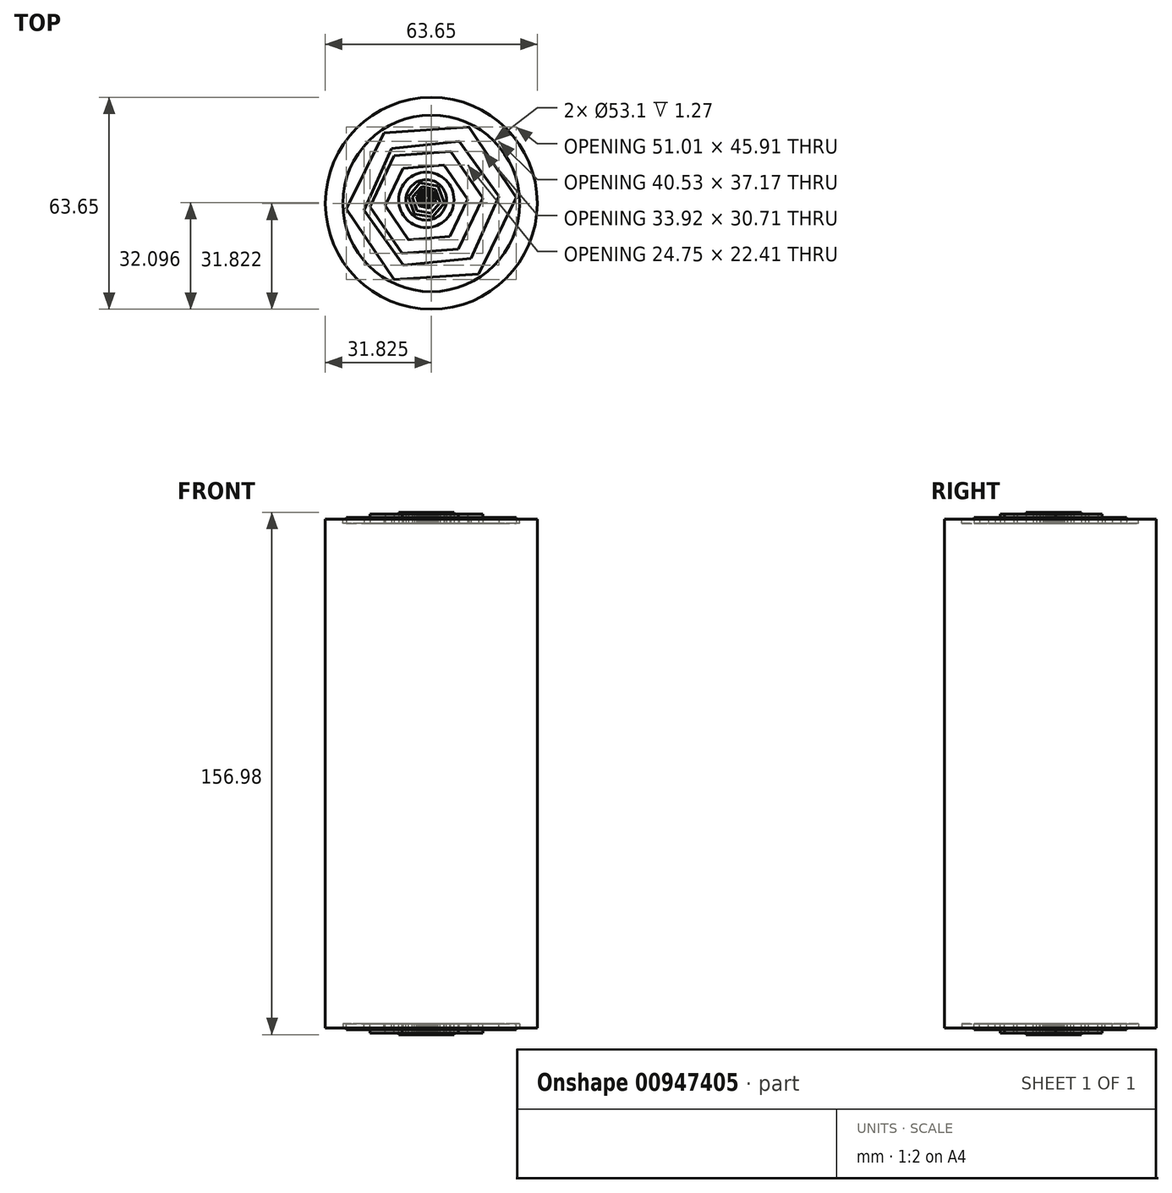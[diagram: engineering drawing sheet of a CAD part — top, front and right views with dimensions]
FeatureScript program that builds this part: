
annotation { "Feature Type Name" : "Feature", "Feature Type Description" : "" }
export const myFeature = defineFeature(function(context is Context, id is Id, definition is map)
    precondition{}
    {
        {
            var Q0;
            Q0=qCreatedBy(makeId("Top.planeOp"),FACE);
            var sketch = newSketch(context, id + "F0", { "sketchPlane" : qUnion([Q0])});
            skLineSegment(sketch, "E0.bottom", {"start": v(-51.93, 60.76) * mm, "end": v(61.08, 60.76) * mm});
            skLineSegment(sketch, "E0.top", {"start": v(-51.93, -63.18) * mm, "end": v(61.08, -63.18) * mm});
            skLineSegment(sketch, "E0.left", {"start": v(-51.93, 60.76) * mm, "end": v(-51.93, -63.18) * mm});
            skLineSegment(sketch, "E0.right", {"start": v(61.08, 60.76) * mm, "end": v(61.08, -63.18) * mm});
            skSolve(sketch);
        }
        {
            var Q0;
            Q0 = qSketchRegion(id + "F0", true);
            var Q1;
            Q1=sQuery(id+"F0.wireOp",EDGE,"E0.left");
            extrude(context, id + "F1", {"entities" : qUnion([Q0]), "surfaceEntities" : qUnion([Q1]), "depth" : 76.45 * mm, "offsetDistance" : 25.4 * mm});
        }
        {
            var Q0;
            Q0=makeQuery(id+"F1.opExtrude","CAP_FACE",FACE,{"disambiguationData":[OSD([sQuery(id+"F0.wireOp",EDGE,"E0.bottom"),sQuery(id+"F0.wireOp",EDGE,"E0.top"),sQuery(id+"F0.wireOp",EDGE,"E0.left"),sQuery(id+"F0.wireOp",EDGE,"E0.right")])],"isStart":false});
            var sketch = newSketch(context, id + "F2", { "sketchPlane" : qUnion([Q0])});
            skLineSegment(sketch, "E1", {"start": v(-51.93, 0) * mm, "end": v(-14.1, 60.76) * mm});
            skPoint(sketch, "E1.startSnap0", {"position": v(-51.93, -1.2) * mm});
            skLineSegment(sketch, "E2", {"start": v(-14.1, 60.76) * mm, "end": v(-51.93, 60.76) * mm});
            skLineSegment(sketch, "E3", {"start": v(-51.93, 60.76) * mm, "end": v(-51.93, -1.2) * mm});
            skSolve(sketch);
        }
        {
            var Q0;
            Q0 = qSketchRegion(id + "F2", true);
            extrude(context, id + "F3", {"entities" : qUnion([Q0]), "operationType" : NewBodyOperationType.REMOVE, "oppositeDirection" : true, "depth" : 101.1 * mm, "offsetDistance" : 25.4 * mm});
        }
        {
            var Q0;
            Q0=makeQuery(id+"F1.opExtrude","CAP_FACE",FACE,{"disambiguationData":[OSD([sQuery(id+"F0.wireOp",EDGE,"E0.bottom"),sQuery(id+"F0.wireOp",EDGE,"E0.top"),sQuery(id+"F0.wireOp",EDGE,"E0.left"),sQuery(id+"F0.wireOp",EDGE,"E0.right")])],"isStart":false});
            var sketch = newSketch(context, id + "F4", { "sketchPlane" : qUnion([Q0])});
            skLineSegment(sketch, "E4", {"start": v(61.08, 0) * mm, "end": v(13.5, 60.76) * mm});
            skLineSegment(sketch, "E5", {"start": v(13.5, 60.76) * mm, "end": v(61.08, 60.76) * mm});
            skLineSegment(sketch, "E6", {"start": v(61.08, 60.76) * mm, "end": v(61.08, 0) * mm});
            skSolve(sketch);
        }
        {
            var Q0;
            Q0 = qSketchRegion(id + "F4", true);
            extrude(context, id + "F5", {"entities" : qUnion([Q0]), "operationType" : NewBodyOperationType.REMOVE, "oppositeDirection" : true, "depth" : 99.57 * mm, "offsetDistance" : 25.4 * mm});
        }
        {
            var Q0;
            Q0=makeQuery(id+"F1.opExtrude","CAP_FACE",FACE,{"disambiguationData":[OSD([sQuery(id+"F0.wireOp",EDGE,"E0.bottom"),sQuery(id+"F0.wireOp",EDGE,"E0.top"),sQuery(id+"F0.wireOp",EDGE,"E0.left"),sQuery(id+"F0.wireOp",EDGE,"E0.right")])],"isStart":false});
            var sketch = newSketch(context, id + "F6", { "sketchPlane" : qUnion([Q0])});
            skLineSegment(sketch, "E7", {"start": v(-51.93, 0) * mm, "end": v(-0.3, 60.76) * mm});
            skLineSegment(sketch, "E8", {"start": v(-0.3, 60.76) * mm, "end": v(61.08, 0) * mm});
            skLineSegment(sketch, "E9", {"start": v(61.08, 0) * mm, "end": v(13.5, 60.76) * mm});
            skLineSegment(sketch, "E10", {"start": v(13.5, 60.76) * mm, "end": v(-14.1, 60.76) * mm});
            skLineSegment(sketch, "E11", {"start": v(-14.1, 60.76) * mm, "end": v(-51.93, 0) * mm});
            skSolve(sketch);
        }
        {
            var Q0;
            Q0 = qSketchRegion(id + "F6", true);
            extrude(context, id + "F7", {"entities" : qUnion([Q0]), "operationType" : NewBodyOperationType.REMOVE, "oppositeDirection" : true, "depth" : 103.38 * mm, "offsetDistance" : 25.4 * mm});
        }
        {
            var Q0;
            Q0=makeQuery(id+"F1.opExtrude","CAP_FACE",FACE,{"disambiguationData":[OSD([sQuery(id+"F0.wireOp",EDGE,"E0.bottom"),sQuery(id+"F0.wireOp",EDGE,"E0.top"),sQuery(id+"F0.wireOp",EDGE,"E0.left"),sQuery(id+"F0.wireOp",EDGE,"E0.right")])],"isStart":false});
            var sketch = newSketch(context, id + "F8", { "sketchPlane" : qUnion([Q0])});
            skLineSegment(sketch, "E12", {"start": v(-11.92, -63.18) * mm, "end": v(-11.92, -38.13) * mm});
            skLineSegment(sketch, "E13", {"start": v(-11.92, -38.13) * mm, "end": v(0, -38.13) * mm});
            skLineSegment(sketch, "E14", {"start": v(0, -38.13) * mm, "end": v(0, -63.18) * mm});
            skLineSegment(sketch, "E15", {"start": v(0, -63.18) * mm, "end": v(12.9, -63.18) * mm});
            skLineSegment(sketch, "E16", {"start": v(12.9, -63.18) * mm, "end": v(12.9, -38.13) * mm});
            skLineSegment(sketch, "E17", {"start": v(12.9, -38.13) * mm, "end": v(0, -38.13) * mm});
            skLineSegment(sketch, "E18", {"start": v(-11.92, -63.18) * mm, "end": v(0, -63.18) * mm});
            skSolve(sketch);
        }
        {
            var Q0;
            Q0 = qSketchRegion(id + "F8", true);
            extrude(context, id + "F9", {"entities" : qUnion([Q0]), "operationType" : NewBodyOperationType.REMOVE, "oppositeDirection" : true, "depth" : 2.3 * mm, "offsetDistance" : 25.4 * mm});
        }
        {
            var Q0;
            {var subQ0=sQuery(id+"F8.wireOp",EDGE,"E12");var subQ1=sQuery(id+"F8.wireOp",EDGE,"E17");var subQ2=sQuery(id+"F8.wireOp",EDGE,"E13");Q0=makeQuery(id+"FAAV3g0l9lUvfrH_1.boolean.opBoolean","SPLIT",FACE,{"disambiguationData":[TD([makeQuery(id+"F9.boolean.opBoolean","COPY",FACE,{"derivedFrom":makeQuery(id+"F9.opExtrude","SWEPT_FACE",FACE,{"disambiguationData":[OSD([subQ0])]})})])],"derivedFrom":makeQuery(id+"F9.boolean.opBoolean","COPY",FACE,{"derivedFrom":makeQuery(id+"F9.opExtrude","CAP_FACE",FACE,{"disambiguationData":[OSD([subQ0,subQ2,sQuery(id+"F8.wireOp",EDGE,"E15"),sQuery(id+"F8.wireOp",EDGE,"E16"),subQ1,sQuery(id+"F8.wireOp",EDGE,"E18")])],"isStart":false})})});}
            var sketch = newSketch(context, id + "F10", { "sketchPlane" : qUnion([Q0])});
            skCircle(sketch, "E19", {"center": v(-1.35, -50.28) * mm, "radius": 0.62 * mm});
            skCircle(sketch, "E20", {"center": v(1.89, -50.24) * mm, "radius": 0.62 * mm});
            skSolve(sketch);
        }
        {
            var Q0;
            Q0 = qSketchRegion(id + "F10", true);
            extrude(context, id + "F11", {"entities" : qUnion([Q0]), "operationType" : NewBodyOperationType.ADD, "depth" : 0.69 * mm, "offsetDistance" : 25.4 * mm});
        }
        {
            var Q0;
            Q0=makeQuery(id+"F1.opExtrude","CAP_FACE",FACE,{"disambiguationData":[OSD([sQuery(id+"F0.wireOp",EDGE,"E0.bottom"),sQuery(id+"F0.wireOp",EDGE,"E0.top"),sQuery(id+"F0.wireOp",EDGE,"E0.left"),sQuery(id+"F0.wireOp",EDGE,"E0.right")])],"isStart":false});
            var sketch = newSketch(context, id + "F12", { "sketchPlane" : qUnion([Q0])});
            skCircle(sketch, "E21", {"center": v(1.5, 13.2) * mm, "radius": 26.55 * mm});
            skSolve(sketch);
        }
        {
            var Q0;
            Q0 = qSketchRegion(id + "F12", true);
            extrude(context, id + "F13", {"entities" : qUnion([Q0]), "operationType" : NewBodyOperationType.REMOVE, "oppositeDirection" : true, "depth" : 1.27 * mm, "offsetDistance" : 25.4 * mm});
        }
        {
            var Q0;
            Q0=makeQuery(id+"F13.boolean.opBoolean","COPY",FACE,{"derivedFrom":makeQuery(id+"F13.opExtrude","CAP_FACE",FACE,{"disambiguationData":[OSD([sQuery(id+"F12.wireOp",EDGE,"E21")])],"isStart":false})});
            var sketch = newSketch(context, id + "F14", { "sketchPlane" : qUnion([Q0])});
            skCircle(sketch, "E22.cCircle", {"center": v(1.5, 13.2) * mm, "radius": 22.14 * mm, "construction": true});
            skLineSegment(sketch, "E22.0", {"start": v(-12.75, 34.42) * mm, "end": v(12.75, 36.16) * mm});
            skLineSegment(sketch, "E22.1", {"start": v(12.75, 36.16) * mm, "end": v(27, 14.94) * mm});
            skLineSegment(sketch, "E22.2", {"start": v(27, 14.94) * mm, "end": v(15.76, -8.02) * mm});
            skLineSegment(sketch, "E22.3", {"start": v(15.76, -8.02) * mm, "end": v(-9.74, -9.75) * mm});
            skLineSegment(sketch, "E22.4", {"start": v(-9.74, -9.75) * mm, "end": v(-24, 11.47) * mm});
            skLineSegment(sketch, "E22.5", {"start": v(-24, 11.47) * mm, "end": v(-12.75, 34.42) * mm});
            skPoint(sketch, "E22.0.midPoint", {"position": v(0, 35.29) * mm});
            skCircle(sketch, "E23.cCircle", {"center": v(1.5, 13.2) * mm, "radius": 17.64 * mm, "construction": true});
            skLineSegment(sketch, "E23.0", {"start": v(-18.76, 11.13) * mm, "end": v(-10.43, 29.71) * mm});
            skLineSegment(sketch, "E23.1", {"start": v(-10.43, 29.71) * mm, "end": v(9.84, 31.79) * mm});
            skLineSegment(sketch, "E23.2", {"start": v(9.84, 31.79) * mm, "end": v(21.77, 15.28) * mm});
            skLineSegment(sketch, "E23.3", {"start": v(21.77, 15.28) * mm, "end": v(13.43, -3.3) * mm});
            skLineSegment(sketch, "E23.4", {"start": v(13.43, -3.3) * mm, "end": v(-6.83, -5.38) * mm});
            skLineSegment(sketch, "E23.5", {"start": v(-6.83, -5.38) * mm, "end": v(-18.76, 11.13) * mm});
            skPoint(sketch, "E23.0.midPoint", {"position": v(-14.6, 20.42) * mm});
            skSolve(sketch);
        }
        {
            var Q0;
            Q0 = qSketchRegion(id + "F14", true);
            extrude(context, id + "F15", {"entities" : qUnion([Q0]), "operationType" : NewBodyOperationType.ADD, "depth" : 1.78 * mm, "offsetDistance" : 25.4 * mm});
        }
        {
            var Q0;
            Q0=makeQuery(id+"F15.boolean.opBoolean","SPLIT",FACE,{"disambiguationData":[TD([makeQuery(id+"F15.opExtrude","SWEPT_FACE",FACE,{"disambiguationData":[OSD([sQuery(id+"F14.wireOp",EDGE,"E23.0")])]})])],"derivedFrom":makeQuery(id+"F13.boolean.opBoolean","COPY",FACE,{"derivedFrom":makeQuery(id+"F13.opExtrude","CAP_FACE",FACE,{"disambiguationData":[OSD([sQuery(id+"F12.wireOp",EDGE,"E21")])],"isStart":false})})});
            var sketch = newSketch(context, id + "F16", { "sketchPlane" : qUnion([Q0])});
            skCircle(sketch, "E24.cCircle", {"center": v(0, 13.48) * mm, "radius": 14.73 * mm, "construction": true});
            skLineSegment(sketch, "E24.0", {"start": v(-7.32, -1.88) * mm, "end": v(-16.96, 12.14) * mm});
            skLineSegment(sketch, "E24.1", {"start": v(-16.96, 12.14) * mm, "end": v(-9.64, 27.5) * mm});
            skLineSegment(sketch, "E24.2", {"start": v(-9.64, 27.5) * mm, "end": v(7.32, 28.83) * mm});
            skLineSegment(sketch, "E24.3", {"start": v(7.32, 28.83) * mm, "end": v(16.96, 14.81) * mm});
            skLineSegment(sketch, "E24.4", {"start": v(16.96, 14.81) * mm, "end": v(9.64, -0.54) * mm});
            skLineSegment(sketch, "E24.5", {"start": v(9.64, -0.54) * mm, "end": v(-7.32, -1.88) * mm});
            skPoint(sketch, "E24.0.midPoint", {"position": v(-12.14, 5.13) * mm});
            skCircle(sketch, "E25.cCircle", {"center": v(0, 13.48) * mm, "radius": 10.75 * mm, "construction": true});
            skLineSegment(sketch, "E25.0", {"start": v(-5.34, 2.27) * mm, "end": v(-12.37, 12.5) * mm});
            skLineSegment(sketch, "E25.1", {"start": v(-12.37, 12.5) * mm, "end": v(-7.03, 23.7) * mm});
            skLineSegment(sketch, "E25.2", {"start": v(-7.03, 23.7) * mm, "end": v(5.34, 24.68) * mm});
            skLineSegment(sketch, "E25.3", {"start": v(5.34, 24.68) * mm, "end": v(12.37, 14.45) * mm});
            skLineSegment(sketch, "E25.4", {"start": v(12.37, 14.45) * mm, "end": v(7.03, 3.25) * mm});
            skLineSegment(sketch, "E25.5", {"start": v(7.03, 3.25) * mm, "end": v(-5.34, 2.27) * mm});
            skPoint(sketch, "E25.0.midPoint", {"position": v(-8.86, 7.39) * mm});
            skSolve(sketch);
        }
        {
            var Q0;
            Q0 = qSketchRegion(id + "F16", true);
            extrude(context, id + "F17", {"entities" : qUnion([Q0]), "operationType" : NewBodyOperationType.ADD, "depth" : 2.8 * mm, "offsetDistance" : 25.4 * mm});
        }
        {
            var Q0;
            Q0=makeQuery(id+"F17.boolean.opBoolean","SPLIT",FACE,{"disambiguationData":[TD([makeQuery(id+"F17.opExtrude","SWEPT_FACE",FACE,{"disambiguationData":[OSD([sQuery(id+"F16.wireOp",EDGE,"E25.0")])]})])],"derivedFrom":makeQuery(id+"F15.boolean.opBoolean","SPLIT",FACE,{"disambiguationData":[TD([makeQuery(id+"F15.opExtrude","SWEPT_FACE",FACE,{"disambiguationData":[OSD([sQuery(id+"F14.wireOp",EDGE,"E23.0")])]})])],"derivedFrom":makeQuery(id+"F13.boolean.opBoolean","COPY",FACE,{"derivedFrom":makeQuery(id+"F13.opExtrude","CAP_FACE",FACE,{"disambiguationData":[OSD([sQuery(id+"F12.wireOp",EDGE,"E21")])],"isStart":false})})})});
            var sketch = newSketch(context, id + "F18", { "sketchPlane" : qUnion([Q0])});
            skCircle(sketch, "E26", {"center": v(0, 14.22) * mm, "radius": 8.33 * mm});
            skCircle(sketch, "E27", {"center": v(0, 14.22) * mm, "radius": 6.1 * mm});
            skSolve(sketch);
        }
        {
            var Q0;
            Q0 = qSketchRegion(id + "F18", true);
            extrude(context, id + "F19", {"entities" : qUnion([Q0]), "operationType" : NewBodyOperationType.ADD, "depth" : 3.3 * mm, "offsetDistance" : 25.4 * mm});
        }
        {
            var Q0;
            Q0=makeQuery(id+"F19.boolean.opBoolean","SPLIT",FACE,{"disambiguationData":[TD([makeQuery(id+"F19.opExtrude","SWEPT_FACE",FACE,{"disambiguationData":[OSD([sQuery(id+"F18.wireOp",EDGE,"E27")])]})])],"derivedFrom":makeQuery(id+"F17.boolean.opBoolean","SPLIT",FACE,{"disambiguationData":[TD([makeQuery(id+"F17.opExtrude","SWEPT_FACE",FACE,{"disambiguationData":[OSD([sQuery(id+"F16.wireOp",EDGE,"E25.0")])]})])],"derivedFrom":makeQuery(id+"F15.boolean.opBoolean","SPLIT",FACE,{"disambiguationData":[TD([makeQuery(id+"F15.opExtrude","SWEPT_FACE",FACE,{"disambiguationData":[OSD([sQuery(id+"F14.wireOp",EDGE,"E23.0")])]})])],"derivedFrom":makeQuery(id+"F13.boolean.opBoolean","COPY",FACE,{"derivedFrom":makeQuery(id+"F13.opExtrude","CAP_FACE",FACE,{"disambiguationData":[OSD([sQuery(id+"F12.wireOp",EDGE,"E21")])],"isStart":false})})})})});
            var sketch = newSketch(context, id + "F20", { "sketchPlane" : qUnion([Q0])});
            skCircle(sketch, "E28.cCircle", {"center": v(0, 14.22) * mm, "radius": 4.75 * mm, "construction": true});
            skLineSegment(sketch, "E28.0", {"start": v(-5.49, 14.02) * mm, "end": v(-2.92, 18.87) * mm});
            skLineSegment(sketch, "E28.1", {"start": v(-2.92, 18.87) * mm, "end": v(2.57, 19.07) * mm});
            skLineSegment(sketch, "E28.2", {"start": v(2.57, 19.07) * mm, "end": v(5.49, 14.42) * mm});
            skLineSegment(sketch, "E28.3", {"start": v(5.49, 14.42) * mm, "end": v(2.92, 9.57) * mm});
            skLineSegment(sketch, "E28.4", {"start": v(2.92, 9.57) * mm, "end": v(-2.57, 9.37) * mm});
            skLineSegment(sketch, "E28.5", {"start": v(-2.57, 9.37) * mm, "end": v(-5.49, 14.02) * mm});
            skPoint(sketch, "E28.0.midPoint", {"position": v(-4.2, 16.44) * mm});
            skCircle(sketch, "E29.cCircle", {"center": v(0, 14.22) * mm, "radius": 3.89 * mm, "construction": true});
            skLineSegment(sketch, "E29.0", {"start": v(-4.49, 14.15) * mm, "end": v(-2.3, 18.07) * mm});
            skLineSegment(sketch, "E29.1", {"start": v(-2.3, 18.07) * mm, "end": v(2.19, 18.14) * mm});
            skLineSegment(sketch, "E29.2", {"start": v(2.19, 18.14) * mm, "end": v(4.49, 14.28) * mm});
            skLineSegment(sketch, "E29.3", {"start": v(4.49, 14.28) * mm, "end": v(2.3, 10.37) * mm});
            skLineSegment(sketch, "E29.4", {"start": v(2.3, 10.37) * mm, "end": v(-2.19, 10.3) * mm});
            skLineSegment(sketch, "E29.5", {"start": v(-2.19, 10.3) * mm, "end": v(-4.49, 14.15) * mm});
            skPoint(sketch, "E29.0.midPoint", {"position": v(-3.4, 16.11) * mm});
            skSolve(sketch);
        }
        {
            var Q0;
            Q0 = qSketchRegion(id + "F20", true);
            extrude(context, id + "F21", {"entities" : qUnion([Q0]), "operationType" : NewBodyOperationType.ADD, "oppositeDirection" : true, "depth" : 3.56 * mm, "offsetDistance" : 25.4 * mm});
        }
        {
            var Q0;
            Q0=makeQuery(id+"F19.boolean.opBoolean","SPLIT",FACE,{"disambiguationData":[TD([makeQuery(id+"F19.opExtrude","SWEPT_FACE",FACE,{"disambiguationData":[OSD([sQuery(id+"F18.wireOp",EDGE,"E27")])]})])],"derivedFrom":makeQuery(id+"F17.boolean.opBoolean","SPLIT",FACE,{"disambiguationData":[TD([makeQuery(id+"F17.opExtrude","SWEPT_FACE",FACE,{"disambiguationData":[OSD([sQuery(id+"F16.wireOp",EDGE,"E25.0")])]})])],"derivedFrom":makeQuery(id+"F15.boolean.opBoolean","SPLIT",FACE,{"disambiguationData":[TD([makeQuery(id+"F15.opExtrude","SWEPT_FACE",FACE,{"disambiguationData":[OSD([sQuery(id+"F14.wireOp",EDGE,"E23.0")])]})])],"derivedFrom":makeQuery(id+"F13.boolean.opBoolean","COPY",FACE,{"derivedFrom":makeQuery(id+"F13.opExtrude","CAP_FACE",FACE,{"disambiguationData":[OSD([sQuery(id+"F12.wireOp",EDGE,"E21")])],"isStart":false})})})})});
            var sketch = newSketch(context, id + "F22", { "sketchPlane" : qUnion([Q0])});
            skCircle(sketch, "E30.cCircle", {"center": v(0, 14.22) * mm, "radius": 4.75 * mm, "construction": true});
            skLineSegment(sketch, "E30.0", {"start": v(-5.4, 15.18) * mm, "end": v(-1.87, 19.37) * mm});
            skLineSegment(sketch, "E30.1", {"start": v(-1.87, 19.37) * mm, "end": v(3.53, 18.41) * mm});
            skLineSegment(sketch, "E30.2", {"start": v(3.53, 18.41) * mm, "end": v(5.4, 13.26) * mm});
            skLineSegment(sketch, "E30.3", {"start": v(5.4, 13.26) * mm, "end": v(1.87, 9.07) * mm});
            skLineSegment(sketch, "E30.4", {"start": v(1.87, 9.07) * mm, "end": v(-3.53, 10.02) * mm});
            skLineSegment(sketch, "E30.5", {"start": v(-3.53, 10.02) * mm, "end": v(-5.4, 15.18) * mm});
            skPoint(sketch, "E30.0.midPoint", {"position": v(-3.63, 17.27) * mm});
            skCircle(sketch, "E31.cCircle", {"center": v(0, 14.22) * mm, "radius": 3.68 * mm, "construction": true});
            skLineSegment(sketch, "E31.0", {"start": v(-4.16, 15.08) * mm, "end": v(-1.33, 18.25) * mm});
            skLineSegment(sketch, "E31.1", {"start": v(-1.33, 18.25) * mm, "end": v(2.82, 17.39) * mm});
            skLineSegment(sketch, "E31.2", {"start": v(2.82, 17.39) * mm, "end": v(4.16, 13.36) * mm});
            skLineSegment(sketch, "E31.3", {"start": v(4.16, 13.36) * mm, "end": v(1.33, 10.2) * mm});
            skLineSegment(sketch, "E31.4", {"start": v(1.33, 10.2) * mm, "end": v(-2.82, 11.05) * mm});
            skLineSegment(sketch, "E31.5", {"start": v(-2.82, 11.05) * mm, "end": v(-4.16, 15.08) * mm});
            skPoint(sketch, "E31.0.midPoint", {"position": v(-2.75, 16.66) * mm});
            skSolve(sketch);
        }
        {
            var Q0;
            Q0 = qSketchRegion(id + "F22", true);
            extrude(context, id + "F23", {"entities" : qUnion([Q0]), "operationType" : NewBodyOperationType.ADD, "depth" : 3.05 * mm, "offsetDistance" : 25.4 * mm});
        }
        {
            var Q0;
            Q0=makeQuery(id+"F23.boolean.opBoolean","SPLIT",FACE,{"disambiguationData":[TD([makeQuery(id+"F23.opExtrude","SWEPT_FACE",FACE,{"disambiguationData":[OSD([sQuery(id+"F22.wireOp",EDGE,"E31.0")])]})])],"derivedFrom":makeQuery(id+"F19.boolean.opBoolean","SPLIT",FACE,{"disambiguationData":[TD([makeQuery(id+"F19.opExtrude","SWEPT_FACE",FACE,{"disambiguationData":[OSD([sQuery(id+"F18.wireOp",EDGE,"E27")])]})])],"derivedFrom":makeQuery(id+"F17.boolean.opBoolean","SPLIT",FACE,{"disambiguationData":[TD([makeQuery(id+"F17.opExtrude","SWEPT_FACE",FACE,{"disambiguationData":[OSD([sQuery(id+"F16.wireOp",EDGE,"E25.0")])]})])],"derivedFrom":makeQuery(id+"F15.boolean.opBoolean","SPLIT",FACE,{"disambiguationData":[TD([makeQuery(id+"F15.opExtrude","SWEPT_FACE",FACE,{"disambiguationData":[OSD([sQuery(id+"F14.wireOp",EDGE,"E23.0")])]})])],"derivedFrom":makeQuery(id+"F13.boolean.opBoolean","COPY",FACE,{"derivedFrom":makeQuery(id+"F13.opExtrude","CAP_FACE",FACE,{"disambiguationData":[OSD([sQuery(id+"F12.wireOp",EDGE,"E21")])],"isStart":false})})})})})});
            var sketch = newSketch(context, id + "F24", { "sketchPlane" : qUnion([Q0])});
            skCircle(sketch, "E32.cCircle", {"center": v(0, 14.62) * mm, "radius": 2.63 * mm, "construction": true});
            skLineSegment(sketch, "E32.0", {"start": v(-2.98, 15.24) * mm, "end": v(-0.96, 17.51) * mm});
            skLineSegment(sketch, "E32.1", {"start": v(-0.96, 17.51) * mm, "end": v(2.02, 16.9) * mm});
            skLineSegment(sketch, "E32.2", {"start": v(2.02, 16.9) * mm, "end": v(2.98, 14) * mm});
            skLineSegment(sketch, "E32.3", {"start": v(2.98, 14) * mm, "end": v(0.96, 11.74) * mm});
            skLineSegment(sketch, "E32.4", {"start": v(0.96, 11.74) * mm, "end": v(-2.02, 12.35) * mm});
            skLineSegment(sketch, "E32.5", {"start": v(-2.02, 12.35) * mm, "end": v(-2.98, 15.24) * mm});
            skPoint(sketch, "E32.0.midPoint", {"position": v(-1.97, 16.38) * mm});
            skCircle(sketch, "E33.cCircle", {"center": v(0, 14.62) * mm, "radius": 1.99 * mm, "construction": true});
            skLineSegment(sketch, "E33.0", {"start": v(-2.27, 14.96) * mm, "end": v(-0.84, 16.76) * mm});
            skLineSegment(sketch, "E33.1", {"start": v(-0.84, 16.76) * mm, "end": v(1.42, 16.42) * mm});
            skLineSegment(sketch, "E33.2", {"start": v(1.42, 16.42) * mm, "end": v(2.27, 14.3) * mm});
            skLineSegment(sketch, "E33.3", {"start": v(2.27, 14.3) * mm, "end": v(0.84, 12.5) * mm});
            skLineSegment(sketch, "E33.4", {"start": v(0.84, 12.5) * mm, "end": v(-1.42, 12.83) * mm});
            skLineSegment(sketch, "E33.5", {"start": v(-1.42, 12.83) * mm, "end": v(-2.27, 14.96) * mm});
            skPoint(sketch, "E33.0.midPoint", {"position": v(-1.56, 15.86) * mm});
            skSolve(sketch);
        }
        {
            var Q0;
            Q0 = qSketchRegion(id + "F24", true);
            extrude(context, id + "F25", {"entities" : qUnion([Q0]), "operationType" : NewBodyOperationType.ADD, "depth" : 2.9 * mm, "offsetDistance" : 25.4 * mm});
        }
        {
            var Q0;
            Q0=makeQuery(id+"F25.boolean.opBoolean","SPLIT",FACE,{"disambiguationData":[TD([makeQuery(id+"F25.opExtrude","SWEPT_FACE",FACE,{"disambiguationData":[OSD([sQuery(id+"F24.wireOp",EDGE,"E33.0")])]})])],"derivedFrom":makeQuery(id+"F23.boolean.opBoolean","SPLIT",FACE,{"disambiguationData":[TD([makeQuery(id+"F23.opExtrude","SWEPT_FACE",FACE,{"disambiguationData":[OSD([sQuery(id+"F22.wireOp",EDGE,"E31.0")])]})])],"derivedFrom":makeQuery(id+"F19.boolean.opBoolean","SPLIT",FACE,{"disambiguationData":[TD([makeQuery(id+"F19.opExtrude","SWEPT_FACE",FACE,{"disambiguationData":[OSD([sQuery(id+"F18.wireOp",EDGE,"E27")])]})])],"derivedFrom":makeQuery(id+"F17.boolean.opBoolean","SPLIT",FACE,{"disambiguationData":[TD([makeQuery(id+"F17.opExtrude","SWEPT_FACE",FACE,{"disambiguationData":[OSD([sQuery(id+"F16.wireOp",EDGE,"E25.0")])]})])],"derivedFrom":makeQuery(id+"F15.boolean.opBoolean","SPLIT",FACE,{"disambiguationData":[TD([makeQuery(id+"F15.opExtrude","SWEPT_FACE",FACE,{"disambiguationData":[OSD([sQuery(id+"F14.wireOp",EDGE,"E23.0")])]})])],"derivedFrom":makeQuery(id+"F13.boolean.opBoolean","COPY",FACE,{"derivedFrom":makeQuery(id+"F13.opExtrude","CAP_FACE",FACE,{"disambiguationData":[OSD([sQuery(id+"F12.wireOp",EDGE,"E21")])],"isStart":false})})})})})})});
            var sketch = newSketch(context, id + "F26", { "sketchPlane" : qUnion([Q0])});
            skCircle(sketch, "E34", {"center": v(0.14, 14.77) * mm, "radius": 1.62 * mm});
            skCircle(sketch, "E35", {"center": v(0.14, 14.77) * mm, "radius": 1.25 * mm});
            skSolve(sketch);
        }
        {
            var Q0;
            Q0 = qSketchRegion(id + "F26", true);
            extrude(context, id + "F27", {"entities" : qUnion([Q0]), "operationType" : NewBodyOperationType.ADD, "depth" : 2.9 * mm, "offsetDistance" : 25.4 * mm});
        }
        {
            var Q0;
            Q0=makeQuery(id+"F27.boolean.opBoolean","SPLIT",FACE,{"disambiguationData":[TD([makeQuery(id+"F27.opExtrude","SWEPT_FACE",FACE,{"disambiguationData":[OSD([sQuery(id+"F26.wireOp",EDGE,"E35")])]})])],"derivedFrom":makeQuery(id+"F25.boolean.opBoolean","SPLIT",FACE,{"disambiguationData":[TD([makeQuery(id+"F25.opExtrude","SWEPT_FACE",FACE,{"disambiguationData":[OSD([sQuery(id+"F24.wireOp",EDGE,"E33.0")])]})])],"derivedFrom":makeQuery(id+"F23.boolean.opBoolean","SPLIT",FACE,{"disambiguationData":[TD([makeQuery(id+"F23.opExtrude","SWEPT_FACE",FACE,{"disambiguationData":[OSD([sQuery(id+"F22.wireOp",EDGE,"E31.0")])]})])],"derivedFrom":makeQuery(id+"F19.boolean.opBoolean","SPLIT",FACE,{"disambiguationData":[TD([makeQuery(id+"F19.opExtrude","SWEPT_FACE",FACE,{"disambiguationData":[OSD([sQuery(id+"F18.wireOp",EDGE,"E27")])]})])],"derivedFrom":makeQuery(id+"F17.boolean.opBoolean","SPLIT",FACE,{"disambiguationData":[TD([makeQuery(id+"F17.opExtrude","SWEPT_FACE",FACE,{"disambiguationData":[OSD([sQuery(id+"F16.wireOp",EDGE,"E25.0")])]})])],"derivedFrom":makeQuery(id+"F15.boolean.opBoolean","SPLIT",FACE,{"disambiguationData":[TD([makeQuery(id+"F15.opExtrude","SWEPT_FACE",FACE,{"disambiguationData":[OSD([sQuery(id+"F14.wireOp",EDGE,"E23.0")])]})])],"derivedFrom":makeQuery(id+"F13.boolean.opBoolean","COPY",FACE,{"derivedFrom":makeQuery(id+"F13.opExtrude","CAP_FACE",FACE,{"disambiguationData":[OSD([sQuery(id+"F12.wireOp",EDGE,"E21")])],"isStart":false})})})})})})})});
            var sketch = newSketch(context, id + "F28", { "sketchPlane" : qUnion([Q0])});
            skCircle(sketch, "E36.cCircle", {"center": v(0.08, 14.82) * mm, "radius": 0.87 * mm, "construction": true});
            skLineSegment(sketch, "E36.0", {"start": v(-0.87, 15.15) * mm, "end": v(-0.11, 15.8) * mm});
            skLineSegment(sketch, "E36.1", {"start": v(-0.11, 15.8) * mm, "end": v(0.84, 15.47) * mm});
            skLineSegment(sketch, "E36.2", {"start": v(0.84, 15.47) * mm, "end": v(1.02, 14.49) * mm});
            skLineSegment(sketch, "E36.3", {"start": v(1.02, 14.49) * mm, "end": v(0.26, 13.83) * mm});
            skLineSegment(sketch, "E36.4", {"start": v(0.26, 13.83) * mm, "end": v(-0.69, 14.17) * mm});
            skLineSegment(sketch, "E36.5", {"start": v(-0.69, 14.17) * mm, "end": v(-0.87, 15.15) * mm});
            skPoint(sketch, "E36.0.midPoint", {"position": v(-0.5, 15.48) * mm});
            skCircle(sketch, "E37.cCircle", {"center": v(0.08, 14.82) * mm, "radius": 0.7 * mm, "construction": true});
            skLineSegment(sketch, "E37.0", {"start": v(-0.7, 15.02) * mm, "end": v(-0.14, 15.6) * mm});
            skLineSegment(sketch, "E37.1", {"start": v(-0.14, 15.6) * mm, "end": v(0.64, 15.4) * mm});
            skLineSegment(sketch, "E37.2", {"start": v(0.64, 15.4) * mm, "end": v(0.85, 14.62) * mm});
            skLineSegment(sketch, "E37.3", {"start": v(0.85, 14.62) * mm, "end": v(0.29, 14.04) * mm});
            skLineSegment(sketch, "E37.4", {"start": v(0.29, 14.04) * mm, "end": v(-0.49, 14.25) * mm});
            skLineSegment(sketch, "E37.5", {"start": v(-0.49, 14.25) * mm, "end": v(-0.7, 15.02) * mm});
            skPoint(sketch, "E37.0.midPoint", {"position": v(-0.42, 15.3) * mm});
            skSolve(sketch);
        }
        {
            var Q0;
            Q0 = qSketchRegion(id + "F28", true);
            extrude(context, id + "F29", {"entities" : qUnion([Q0]), "operationType" : NewBodyOperationType.ADD, "depth" : 2.7 * mm, "offsetDistance" : 25.4 * mm});
        }
        {
            var Q0;
            Q0=makeQuery(id+"F1.opExtrude","CAP_FACE",FACE,{"disambiguationData":[OSD([sQuery(id+"F0.wireOp",EDGE,"E0.bottom"),sQuery(id+"F0.wireOp",EDGE,"E0.top"),sQuery(id+"F0.wireOp",EDGE,"E0.left"),sQuery(id+"F0.wireOp",EDGE,"E0.right")])],"isStart":false});
            var sketch = newSketch(context, id + "F30", { "sketchPlane" : qUnion([Q0])});
            skCircle(sketch, "E38", {"center": v(1.5, 13.2) * mm, "radius": 31.83 * mm});
            skCircle(sketch, "E39", {"center": v(1.5, 13.2) * mm, "radius": 98.41 * mm});
            skSolve(sketch);
        }
        {
            var Q0;
            Q0 = qSketchRegion(id + "F30", true);
            extrude(context, id + "F31", {"entities" : qUnion([Q0]), "operationType" : NewBodyOperationType.REMOVE, "oppositeDirection" : true, "depth" : 92.96 * mm, "offsetDistance" : 25.4 * mm});
        }
        {
            var Q0;
            Q0=makeQuery(id+"F31.boolean.opBoolean","SPLIT",BODY,{"disambiguationData":[OD(1.0)],"derivedFrom":makeQuery(id+"F1.opExtrude","SWEPT_BODY",BODY,{"disambiguationData":[OSD([sQuery(id+"F0.wireOp",EDGE,"E0.bottom"),sQuery(id+"F0.wireOp",EDGE,"E0.top"),sQuery(id+"F0.wireOp",EDGE,"E0.left"),sQuery(id+"F0.wireOp",EDGE,"E0.right")])]})});
            var Q1;
            Q1=qCreatedBy(makeId("Top.planeOp"),FACE);
            mirror(context, id + "F32", {"operationType" : NewBodyOperationType.ADD, "entities" : qUnion([Q0]), "mirrorPlane" : qUnion([Q1])});
        }
    });
